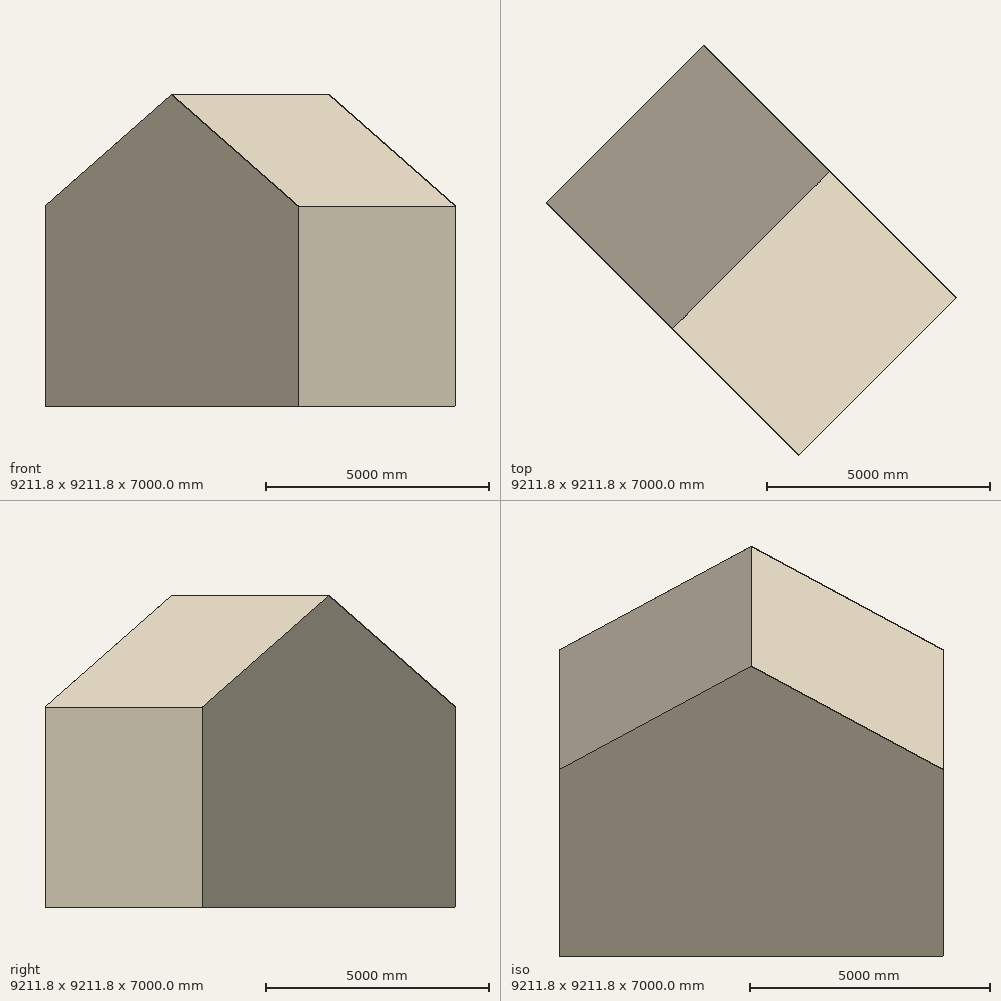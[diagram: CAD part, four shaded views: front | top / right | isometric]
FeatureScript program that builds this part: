
annotation { "Feature Type Name" : "Feature", "Feature Type Description" : "" }
export const myFeature = defineFeature(function(context is Context, id is Id, definition is map)
    precondition{}
    {
        {
            var Q0;
            Q0=qCreatedBy(makeId("Front.planeOp"),FACE);
            var sketch = newSketch(context, id + "F0", { "sketchPlane" : qUnion([Q0])});
            skLineSegment(sketch, "E0", {"start": v(0, 0) * mm, "end": v(0, 78.2) * mm, "construction": true});
            skLineSegment(sketch, "E1", {"start": v(0, 0) * mm, "end": v(-107.34, 0) * mm, "construction": true});
            skSolve(sketch);
        }
        {
            var Q0;
            Q0=qCreatedBy(makeId("Top.planeOp"),FACE);
            var sketch = newSketch(context, id + "F1", { "sketchPlane" : qUnion([Q0])});
            skLineSegment(sketch, "E2", {"start": v(0, 0) * mm, "end": v(-77.42, -77.42) * mm, "construction": true});
            skLineSegment(sketch, "E3", {"start": v(0, 0) * mm, "end": v(-57.52, 57.52) * mm, "construction": true});
            skSolve(sketch);
        }
        {
            var Q0;
            Q0=sQuery(id+"F0.wireOp",VERTEX,"E0.end");
            var Q1;
            Q1=sQuery(id+"F1.wireOp",VERTEX,"E2.start");
            var Q2;
            Q2=sQuery(id+"F1.wireOp",VERTEX,"E3.end");
            cPlane(context, id + "F2", {"entities" : qUnion([Q0, Q1, Q2]), "cplaneType" : CPlaneType.THREE_POINT, "offset" : 25 * mm, "width" : 150 * mm, "height" : 150 * mm});
        }
        {
            var Q0;
            Q0=qCreatedBy(id+"F2.planeOp",FACE);
            var sketch = newSketch(context, id + "F3", { "sketchPlane" : qUnion([Q0])});
            skLineSegment(sketch, "E4", {"start": v(0, 2500) * mm, "end": v(-4013.72, 0) * mm});
            skLineSegment(sketch, "E5", {"start": v(0, 2500) * mm, "end": v(0, 0) * mm, "construction": true});
            skLineSegment(sketch, "E6", {"start": v(-4013.72, 0) * mm, "end": v(-4013.72, -4500) * mm});
            skLineSegment(sketch, "E7.MirrorCS", {"start": v(0, 2500) * mm, "end": v(4013.72, 0) * mm});
            skLineSegment(sketch, "E8.MirrorCS", {"start": v(4013.72, 0) * mm, "end": v(4013.72, -4500) * mm});
            skLineSegment(sketch, "E9", {"start": v(4013.72, -4500) * mm, "end": v(-4013.72, -4500) * mm});
            skSolve(sketch);
        }
        {
            var Q0;
            Q0=qSketchRegion(id+"F3",true);
            extrude(context, id + "F4", {"entities" : qUnion([Q0]), "endBound" : BoundingType.SYMMETRIC, "depth" : 5000 * mm});
        }
    });
